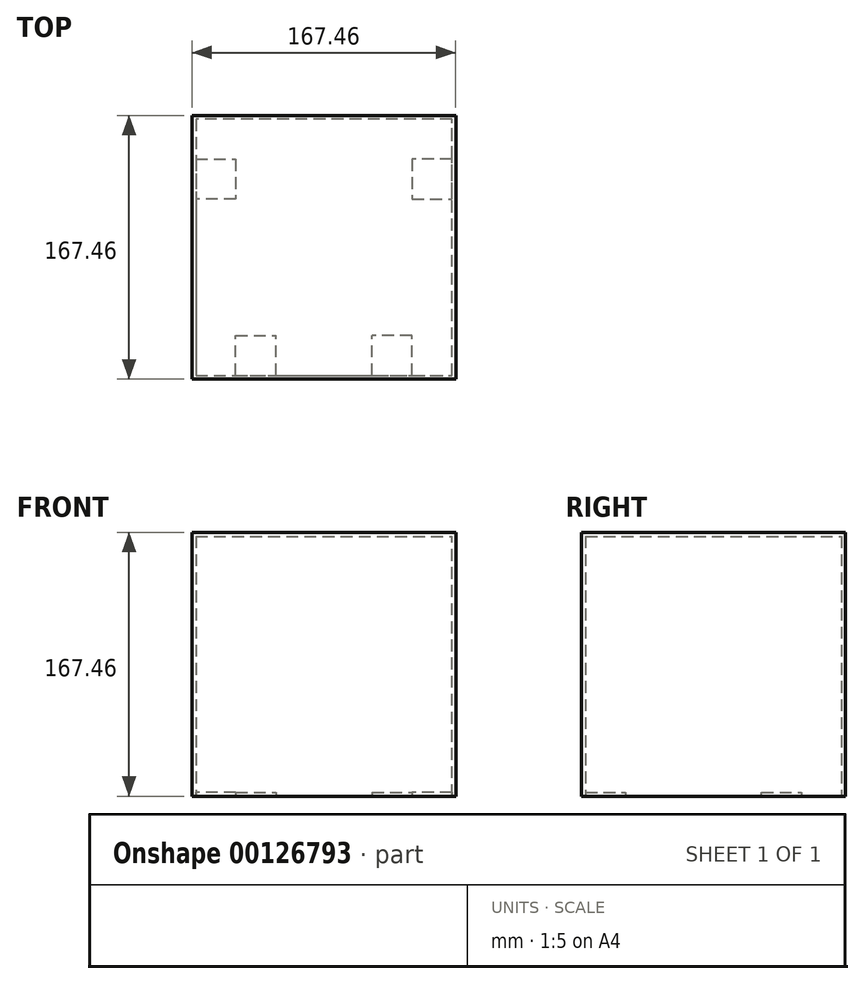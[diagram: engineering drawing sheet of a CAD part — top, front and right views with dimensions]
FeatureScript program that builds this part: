
annotation { "Feature Type Name" : "Feature", "Feature Type Description" : "" }
export const myFeature = defineFeature(function(context is Context, id is Id, definition is map)
    precondition{}
    {
        {
            var Q0;
            Q0=qCreatedBy(makeId("Front.planeOp"),FACE);
            var sketch = newSketch(context, id + "F0", { "sketchPlane" : qUnion([Q0])});
            skLineSegment(sketch, "E0.bottom", {"start": v(0, 0) * mm, "end": v(165.1, 0) * mm});
            skLineSegment(sketch, "E0.top", {"start": v(0, 165.1) * mm, "end": v(165.1, 165.1) * mm});
            skLineSegment(sketch, "E0.left", {"start": v(0, 0) * mm, "end": v(0, 165.1) * mm});
            skLineSegment(sketch, "E0.right", {"start": v(165.1, 0) * mm, "end": v(165.1, 165.1) * mm});
            skSolve(sketch);
        }
        {
            var Q0;
            Q0=makeQuery(id+"F0.imprint","IMPRINT",FACE,{"disambiguationData":[TD([[makeQuery(id+"F0.imprint","IMPRINT",EDGE,{"derivedFrom":sQuery(id+"F0.wireOp",EDGE,"E0.bottom")}),1.0]])]});
            extrude(context, id + "F1", {"entities" : qUnion([Q0]), "depth" : 2.36 * mm});
        }
        {
            var Q0;
            Q0=makeQuery(id+"F1.opExtrude","SWEPT_FACE",FACE,{"disambiguationData":[OSD([sQuery(id+"F0.wireOp",EDGE,"E0.right")])]});
            var sketch = newSketch(context, id + "F2", { "sketchPlane" : qUnion([Q0])});
            skLineSegment(sketch, "E1.bottom", {"start": v(-2.36, 165.1) * mm, "end": v(162.74, 165.1) * mm});
            skLineSegment(sketch, "E1.top", {"start": v(-2.36, 0) * mm, "end": v(162.74, 0) * mm});
            skLineSegment(sketch, "E1.left", {"start": v(-2.36, 165.1) * mm, "end": v(-2.36, 0) * mm});
            skLineSegment(sketch, "E1.right", {"start": v(162.74, 165.1) * mm, "end": v(162.74, 0) * mm});
            skSolve(sketch);
        }
        {
            var Q0;
            {var subQ2=sQuery(id+"F2.wireOp",EDGE,"E1.left");Q0=makeQuery(id+"F2.imprint","IMPRINT",FACE,{"disambiguationData":[TD([[makeQuery(id+"F2.imprint","IMPRINT",EDGE,{"derivedFrom":subQ2}),-1.0]])]});}
            var Q1;
            {var subQ2=sQuery(id+"F2.wireOp",EDGE,"E1.right");Q1=makeQuery(id+"F2.imprint","IMPRINT",FACE,{"disambiguationData":[TD([[makeQuery(id+"F2.imprint","IMPRINT",EDGE,{"derivedFrom":subQ2}),-1.0]])]});}
            extrude(context, id + "F3", {"entities" : qUnion([Q0, Q1]), "operationType" : NewBodyOperationType.ADD, "depth" : 2.36 * mm});
        }
        {
            var Q0;
            Q0=makeQuery(id+"F3.opExtrude","SWEPT_FACE",FACE,{"disambiguationData":[OSD([sQuery(id+"F2.wireOp",EDGE,"E1.right")])]});
            var sketch = newSketch(context, id + "F4", { "sketchPlane" : qUnion([Q0])});
            skLineSegment(sketch, "E2.bottom", {"start": v(-167.46, 165.1) * mm, "end": v(-2.36, 165.1) * mm});
            skLineSegment(sketch, "E2.top", {"start": v(-167.46, 0) * mm, "end": v(-2.36, 0) * mm});
            skLineSegment(sketch, "E2.left", {"start": v(-167.46, 165.1) * mm, "end": v(-167.46, 0) * mm});
            skLineSegment(sketch, "E2.right", {"start": v(-2.36, 165.1) * mm, "end": v(-2.36, 0) * mm});
            skSolve(sketch);
        }
        {
            var Q0;
            {var subQ2=sQuery(id+"F4.wireOp",EDGE,"E2.right");Q0=makeQuery(id+"F4.imprint","IMPRINT",FACE,{"disambiguationData":[TD([[makeQuery(id+"F4.imprint","IMPRINT",EDGE,{"derivedFrom":subQ2}),-1.0]])]});}
            var Q1;
            {var subQ2=sQuery(id+"F4.wireOp",EDGE,"E2.left");Q1=makeQuery(id+"F4.imprint","IMPRINT",FACE,{"disambiguationData":[TD([[makeQuery(id+"F4.imprint","IMPRINT",EDGE,{"derivedFrom":subQ2}),1.0]])]});}
            extrude(context, id + "F5", {"entities" : qUnion([Q0, Q1]), "operationType" : NewBodyOperationType.ADD, "depth" : 2.36 * mm});
        }
        {
            var Q0;
            Q0=makeQuery(id+"F5.opExtrude","SWEPT_FACE",FACE,{"disambiguationData":[OSD([sQuery(id+"F4.wireOp",EDGE,"E2.right")])]});
            var sketch = newSketch(context, id + "F6", { "sketchPlane" : qUnion([Q0])});
            skLineSegment(sketch, "E3.bottom", {"start": v(-165.1, 165.1) * mm, "end": v(0, 165.1) * mm});
            skLineSegment(sketch, "E3.top", {"start": v(-165.1, 0) * mm, "end": v(0, 0) * mm});
            skLineSegment(sketch, "E3.left", {"start": v(-165.1, 165.1) * mm, "end": v(-165.1, 0) * mm});
            skLineSegment(sketch, "E3.right", {"start": v(0, 165.1) * mm, "end": v(0, 0) * mm});
            skSolve(sketch);
        }
        {
            var Q0;
            {var subQ2=sQuery(id+"F6.wireOp",EDGE,"E3.right");Q0=makeQuery(id+"F6.imprint","IMPRINT",FACE,{"disambiguationData":[TD([[makeQuery(id+"F6.imprint","IMPRINT",EDGE,{"derivedFrom":subQ2}),-1.0]])]});}
            var Q1;
            {var subQ2=sQuery(id+"F6.wireOp",EDGE,"E3.left");Q1=makeQuery(id+"F6.imprint","IMPRINT",FACE,{"disambiguationData":[TD([[makeQuery(id+"F6.imprint","IMPRINT",EDGE,{"derivedFrom":subQ2}),1.0]])]});}
            extrude(context, id + "F7", {"entities" : qUnion([Q0, Q1]), "operationType" : NewBodyOperationType.ADD, "depth" : 2.36 * mm});
        }
        {
            var Q0;
            Q0=makeQuery(id+"F7.boolean.opBoolean","MERGE",FACE,{"derivedFrom":[makeQuery(id+"F5.boolean.opBoolean","MERGE",FACE,{"derivedFrom":[makeQuery(id+"F3.boolean.opBoolean","MERGE",FACE,{"derivedFrom":[makeQuery(id+"F1.opExtrude","SWEPT_FACE",FACE,{"disambiguationData":[OSD([sQuery(id+"F0.wireOp",EDGE,"E0.top")])]}),makeQuery(id+"F3.opExtrude","SWEPT_FACE",FACE,{"disambiguationData":[OSD([sQuery(id+"F2.wireOp",EDGE,"E1.bottom")])]})]}),makeQuery(id+"F5.opExtrude","SWEPT_FACE",FACE,{"disambiguationData":[OSD([sQuery(id+"F4.wireOp",EDGE,"E2.bottom")])]})]}),makeQuery(id+"F7.opExtrude","SWEPT_FACE",FACE,{"disambiguationData":[OSD([sQuery(id+"F6.wireOp",EDGE,"E3.bottom")])]})]});
            var sketch = newSketch(context, id + "F8", { "sketchPlane" : qUnion([Q0])});
            skLineSegment(sketch, "E4.bottom", {"start": v(0, 165.1) * mm, "end": v(167.46, 165.1) * mm});
            skLineSegment(sketch, "E4.top", {"start": v(0, -2.36) * mm, "end": v(167.46, -2.36) * mm});
            skLineSegment(sketch, "E4.left", {"start": v(0, 165.1) * mm, "end": v(0, -2.36) * mm});
            skLineSegment(sketch, "E4.right", {"start": v(167.46, 165.1) * mm, "end": v(167.46, -2.36) * mm});
            skSolve(sketch);
        }
        {
            var Q0;
            Q0=makeQuery(id+"F8.imprint","IMPRINT",FACE,{"disambiguationData":[TD([[makeQuery(id+"F8.imprint","IMPRINT",EDGE,{"derivedFrom":makeQuery(id+"F3.opExtrude","CAP_EDGE",EDGE,{"disambiguationData":[OSD([sQuery(id+"F2.wireOp",EDGE,"E1.bottom")])],"isStart":true})}),1.0]])]});
            var Q1;
            Q1=makeQuery(id+"F8.imprint","IMPRINT",FACE,{"disambiguationData":[TD([[makeQuery(id+"F8.imprint","IMPRINT",EDGE,{"derivedFrom":sQuery(id+"F8.wireOp",EDGE,"E4.bottom")}),1.0]])]});
            extrude(context, id + "F9", {"entities" : qUnion([Q0, Q1]), "operationType" : NewBodyOperationType.ADD, "depth" : 2.36 * mm});
        }
        {
            var Q0;
            Q0=makeQuery(id+"F7.boolean.opBoolean","MERGE",FACE,{"derivedFrom":[makeQuery(id+"F5.boolean.opBoolean","MERGE",FACE,{"derivedFrom":[makeQuery(id+"F3.boolean.opBoolean","MERGE",FACE,{"derivedFrom":[makeQuery(id+"F1.opExtrude","SWEPT_FACE",FACE,{"disambiguationData":[OSD([sQuery(id+"F0.wireOp",EDGE,"E0.bottom")])]}),makeQuery(id+"F3.opExtrude","SWEPT_FACE",FACE,{"disambiguationData":[OSD([sQuery(id+"F2.wireOp",EDGE,"E1.top")])]})]}),makeQuery(id+"F5.opExtrude","SWEPT_FACE",FACE,{"disambiguationData":[OSD([sQuery(id+"F4.wireOp",EDGE,"E2.top")])]})]}),makeQuery(id+"F7.opExtrude","SWEPT_FACE",FACE,{"disambiguationData":[OSD([sQuery(id+"F6.wireOp",EDGE,"E3.top")])]})]});
            var sketch = newSketch(context, id + "F10", { "sketchPlane" : qUnion([Q0])});
            skLineSegment(sketch, "E5", {"start": v(165.1, -162.74) * mm, "end": v(165.1, -137.34) * mm});
            skLineSegment(sketch, "E6.bottom", {"start": v(165.1, -137.34) * mm, "end": v(139.7, -137.34) * mm});
            skLineSegment(sketch, "E6.right", {"start": v(139.7, -137.34) * mm, "end": v(139.7, -111.94) * mm});
            skLineSegment(sketch, "E7", {"start": v(165.1, 0) * mm, "end": v(139.7, 0) * mm});
            skLineSegment(sketch, "E8.top", {"start": v(139.7, -25.4) * mm, "end": v(114.3, -25.4) * mm});
            skLineSegment(sketch, "E8.left", {"start": v(139.7, 0) * mm, "end": v(139.7, -25.4) * mm});
            skLineSegment(sketch, "E8.right", {"start": v(114.3, 0) * mm, "end": v(114.3, -25.4) * mm});
            skLineSegment(sketch, "E9", {"start": v(114.3, 0) * mm, "end": v(114.3, 2.36) * mm});
            skLineSegment(sketch, "E10", {"start": v(139.7, 0) * mm, "end": v(139.7, 2.36) * mm});
            skLineSegment(sketch, "E11", {"start": v(165.1, -137.34) * mm, "end": v(167.46, -137.34) * mm});
            skLineSegment(sketch, "E12", {"start": v(83.73, 0) * mm, "end": v(83.73, -162.74) * mm});
            skLineSegment(sketch, "E13", {"start": v(139.7, -111.94) * mm, "end": v(165.1, -111.94) * mm});
            skLineSegment(sketch, "E14", {"start": v(165.1, -111.94) * mm, "end": v(167.46, -111.94) * mm});
            skLineSegment(sketch, "E15.MirrorCS", {"start": v(2.36, -137.34) * mm, "end": v(0, -137.34) * mm});
            skLineSegment(sketch, "E16.MirrorCS", {"start": v(27.76, 0) * mm, "end": v(27.76, 2.36) * mm});
            skLineSegment(sketch, "E17.MirrorCS", {"start": v(2.36, -111.94) * mm, "end": v(0, -111.94) * mm});
            skLineSegment(sketch, "E18.MirrorCS", {"start": v(53.16, 0) * mm, "end": v(53.16, 2.36) * mm});
            skLineSegment(sketch, "E19.MirrorCS", {"start": v(27.76, -25.4) * mm, "end": v(53.16, -25.4) * mm});
            skLineSegment(sketch, "E20.MirrorCS", {"start": v(27.76, 0) * mm, "end": v(27.76, -25.4) * mm});
            skLineSegment(sketch, "E21.MirrorCS", {"start": v(53.16, 0) * mm, "end": v(53.16, -25.4) * mm});
            skLineSegment(sketch, "E22.MirrorCS", {"start": v(2.36, -162.74) * mm, "end": v(2.36, -137.34) * mm});
            skLineSegment(sketch, "E23.MirrorCS", {"start": v(27.76, -111.94) * mm, "end": v(2.36, -111.94) * mm});
            skLineSegment(sketch, "E24.MirrorCS", {"start": v(2.36, 0) * mm, "end": v(27.76, 0) * mm});
            skLineSegment(sketch, "E25.MirrorCS", {"start": v(2.36, -137.34) * mm, "end": v(27.76, -137.34) * mm});
            skLineSegment(sketch, "E26.MirrorCS", {"start": v(27.76, -137.34) * mm, "end": v(27.76, -111.94) * mm});
            skSolve(sketch);
        }
        {
            var Q0;
            Q0=makeQuery(id+"F10.imprint","IMPRINT",FACE,{"disambiguationData":[TD([[makeQuery(id+"F10.imprint","IMPRINT",EDGE,{"derivedFrom":sQuery(id+"F10.wireOp",EDGE,"E8.top")}),-1.0]])]});
            var Q1;
            {var subQ0=sQuery(id+"F10.wireOp",EDGE,"E6.bottom");Q1=makeQuery(id+"F10.imprint","IMPRINT",FACE,{"disambiguationData":[TD([[makeQuery(id+"F10.imprint","IMPRINT",EDGE,{"derivedFrom":subQ0}),-1.0]])]});}
            var Q2;
            Q2=makeQuery(id+"F10.imprint","IMPRINT",FACE,{"disambiguationData":[TD([[makeQuery(id+"F10.imprint","IMPRINT",EDGE,{"derivedFrom":sQuery(id+"F10.wireOp",EDGE,"E19.MirrorCS")}),1.0]])]});
            var Q3;
            {var subQ0=sQuery(id+"F10.wireOp",EDGE,"E23.MirrorCS");Q3=makeQuery(id+"F10.imprint","IMPRINT",FACE,{"disambiguationData":[TD([[makeQuery(id+"F10.imprint","IMPRINT",EDGE,{"derivedFrom":subQ0}),1.0]])]});}
            var Q4;
            {var subQ0=sQuery(id+"F10.wireOp",EDGE,"E16.MirrorCS");Q4=makeQuery(id+"F10.imprint","IMPRINT",FACE,{"disambiguationData":[TD([[makeQuery(id+"F10.imprint","IMPRINT",EDGE,{"derivedFrom":subQ0}),-1.0]])]});}
            var Q5;
            {var subQ0=sQuery(id+"F10.wireOp",EDGE,"E9");Q5=makeQuery(id+"F10.imprint","IMPRINT",FACE,{"disambiguationData":[TD([[makeQuery(id+"F10.imprint","IMPRINT",EDGE,{"derivedFrom":subQ0}),-1.0]])]});}
            var Q6;
            {var subQ0=sQuery(id+"F10.wireOp",EDGE,"E15.MirrorCS");Q6=makeQuery(id+"F10.imprint","IMPRINT",FACE,{"disambiguationData":[TD([[makeQuery(id+"F10.imprint","IMPRINT",EDGE,{"derivedFrom":subQ0}),-1.0]])]});}
            var Q7;
            {var subQ0=sQuery(id+"F10.wireOp",EDGE,"E11");Q7=makeQuery(id+"F10.imprint","IMPRINT",FACE,{"disambiguationData":[TD([[makeQuery(id+"F10.imprint","IMPRINT",EDGE,{"derivedFrom":subQ0}),1.0]])]});}
            extrude(context, id + "F11", {"entities" : qUnion([Q0, Q1, Q2, Q3, Q4, Q5, Q6, Q7]), "operationType" : NewBodyOperationType.ADD, "oppositeDirection" : true, "depth" : 2.36 * mm});
        }
    });
